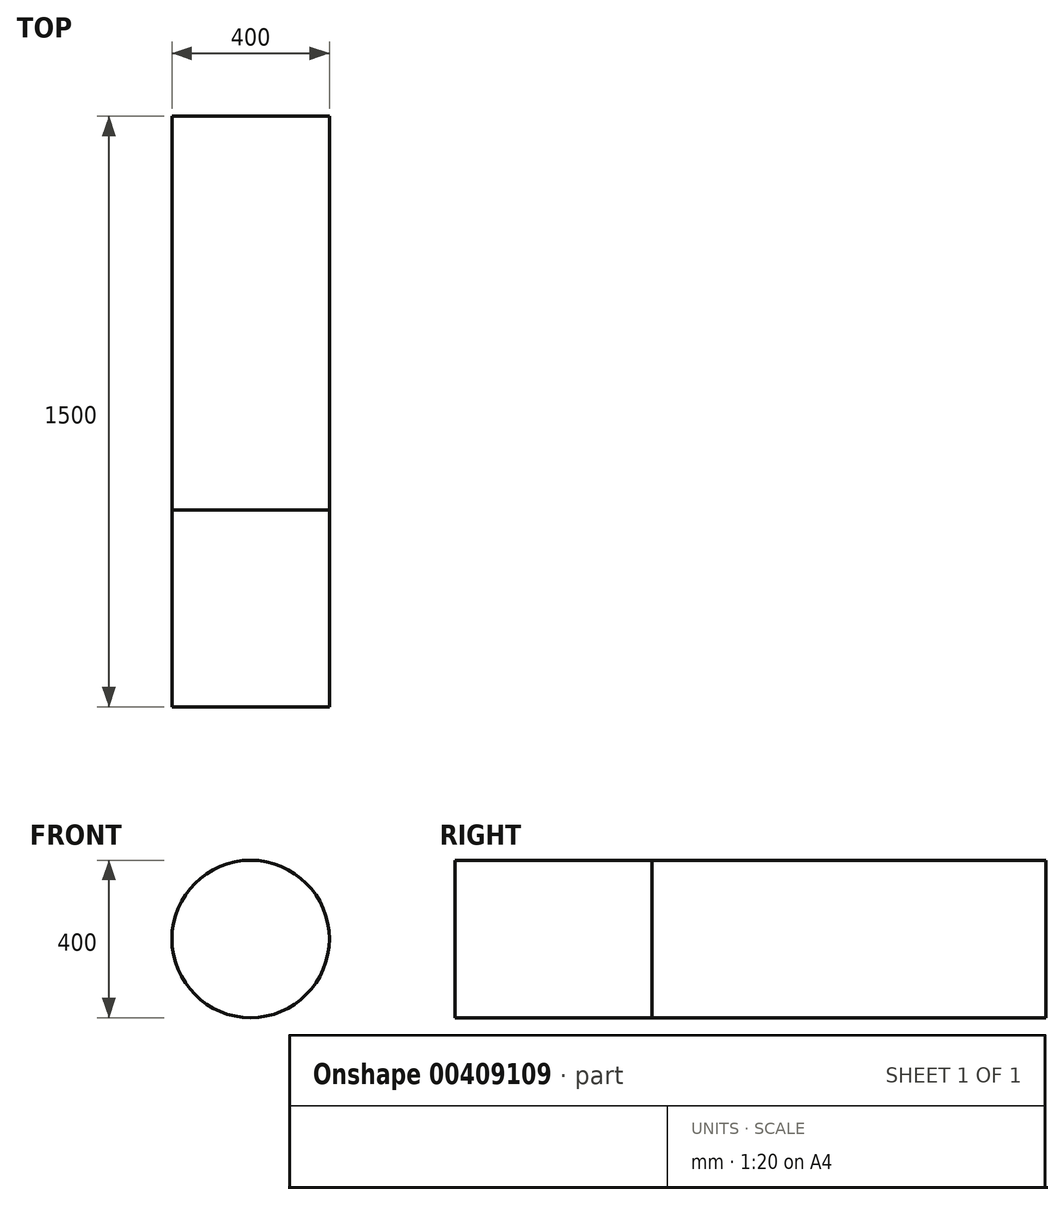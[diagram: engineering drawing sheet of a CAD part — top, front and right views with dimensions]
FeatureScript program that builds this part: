
annotation { "Feature Type Name" : "Feature", "Feature Type Description" : "" }
export const myFeature = defineFeature(function(context is Context, id is Id, definition is map)
    precondition{}
    {
        {
            var Q0;
            Q0=qCreatedBy(makeId("Front.planeOp"),FACE);
            var sketch = newSketch(context, id + "F0", { "sketchPlane" : qUnion([Q0])});
            skCircle(sketch, "E0", {"center": v(3.9, -4.32) * mm, "radius": 200 * mm});
            skSolve(sketch);
        }
        {
            var Q0;
            Q0 = qSketchRegion(id + "F0", true);
            var Q1;
            Q1 = qSketchRegion(id + "FYNlj8a77JiWRND_0", true);
            extrude(context, id + "F1", {"entities" : qUnion([Q0, Q1]), "depth" : 1000 * mm});
        }
        {
            var Q0;
            Q0=makeQuery(id+"F1.opExtrude","CAP_FACE",FACE,{"disambiguationData":[OSD([sQuery(id+"F0.wireOp",EDGE,"E0")])],"isStart":false});
            var sketch = newSketch(context, id + "F2", { "sketchPlane" : qUnion([Q0])});
            skCircle(sketch, "E1", {"center": v(3.9, -4.32) * mm, "radius": 200 * mm});
            skSolve(sketch);
        }
        {
            var Q0;
            Q0 = qSketchRegion(id + "F2", true);
            extrude(context, id + "F3", {"entities" : qUnion([Q0]), "depth" : 500 * mm});
        }
    });
